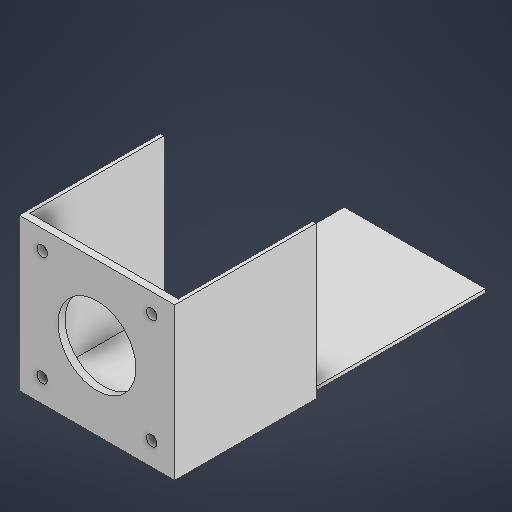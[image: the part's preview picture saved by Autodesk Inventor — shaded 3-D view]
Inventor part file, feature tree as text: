
AUTODESK INVENTOR PART (.ipt)
format: ipt  version: 2025.3 (Build 293356030, 356C)  size: 219,136 bytes
history: native  units: mm
features: sketch x3, extrude x3
ambient origin geometry x8: Origin, YZ Plane, XZ Plane, XY Plane, X Axis, Y Axis, Z Axis, Center Point
bodies: Solid1 (feature_tree)
feature tree (6):
  sketch  "Sketch1"  dims[d0=44.0mm d1=2.95mm]
  extrude  "Extrusion1"  Depth=44.0mm
  extrude  "Extrusion2"  Depth=22.0mm
  extrude  "Extrusion3"  Depth=2.0mm TaperAngle=0.0deg
  sketch  "Sketch Rectangular Pattern1"  dims[d2=20.0mm d4=31.0mm d5=20.0mm d7=31.0mm d10=22.0mm]
  sketch  "Sketch2"  dims[d11=42.0mm d12=2.0mm d13=0.0mm d14=38.0mm d15=0.0mm d16=40.0mm d17=50.0mm d18=0.0mm d19=0.872665mm]
